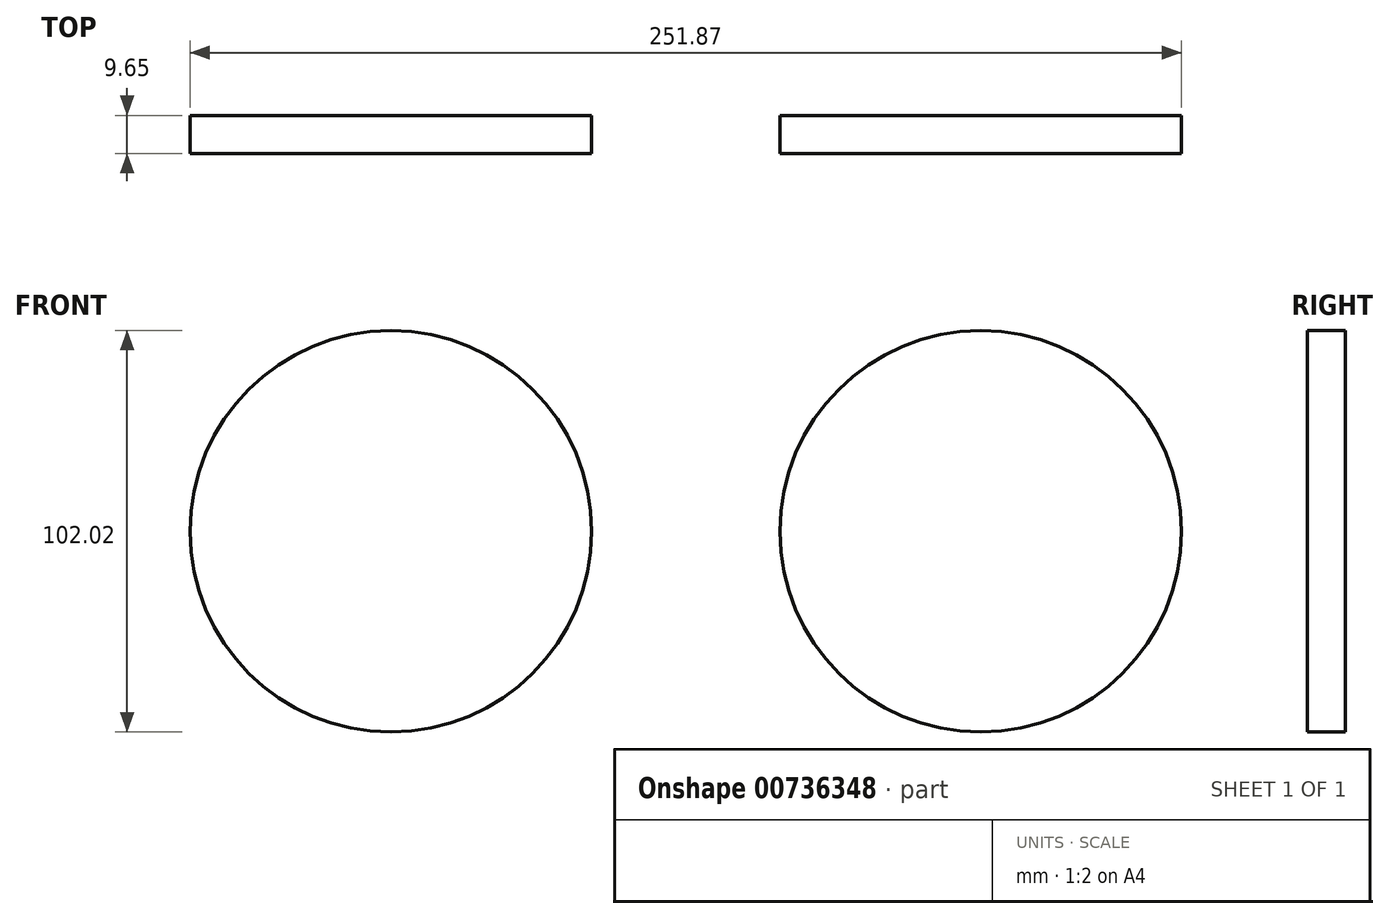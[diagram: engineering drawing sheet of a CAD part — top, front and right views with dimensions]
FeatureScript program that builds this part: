
annotation { "Feature Type Name" : "Feature", "Feature Type Description" : "" }
export const myFeature = defineFeature(function(context is Context, id is Id, definition is map)
    precondition{}
    {
        {
            var Q0;
            Q0=qCreatedBy(makeId("Front.planeOp"),FACE);
            var sketch = newSketch(context, id + "F0", { "sketchPlane" : qUnion([Q0])});
            skCircle(sketch, "E0", {"center": v(-81.55, 0) * mm, "radius": 51 * mm});
            skCircle(sketch, "E1", {"center": v(68.3, 0) * mm, "radius": 51 * mm});
            skSolve(sketch);
        }
        {
            var Q0;
            Q0=makeQuery(id+"F0.imprint","IMPRINT",FACE,{"disambiguationData":[TD([[makeQuery(id+"F0.imprint","IMPRINT",EDGE,{"derivedFrom":sQuery(id+"F0.wireOp",EDGE,"E0")}),1.0]])]});
            var Q1;
            Q1=makeQuery(id+"F0.imprint","IMPRINT",FACE,{"disambiguationData":[TD([[makeQuery(id+"F0.imprint","IMPRINT",EDGE,{"derivedFrom":sQuery(id+"F0.wireOp",EDGE,"E1")}),1.0]])]});
            extrude(context, id + "F1", {"entities" : qUnion([Q0, Q1]), "depth" : 9.65 * mm, "offsetDistance" : 25.4 * mm});
        }
    });
